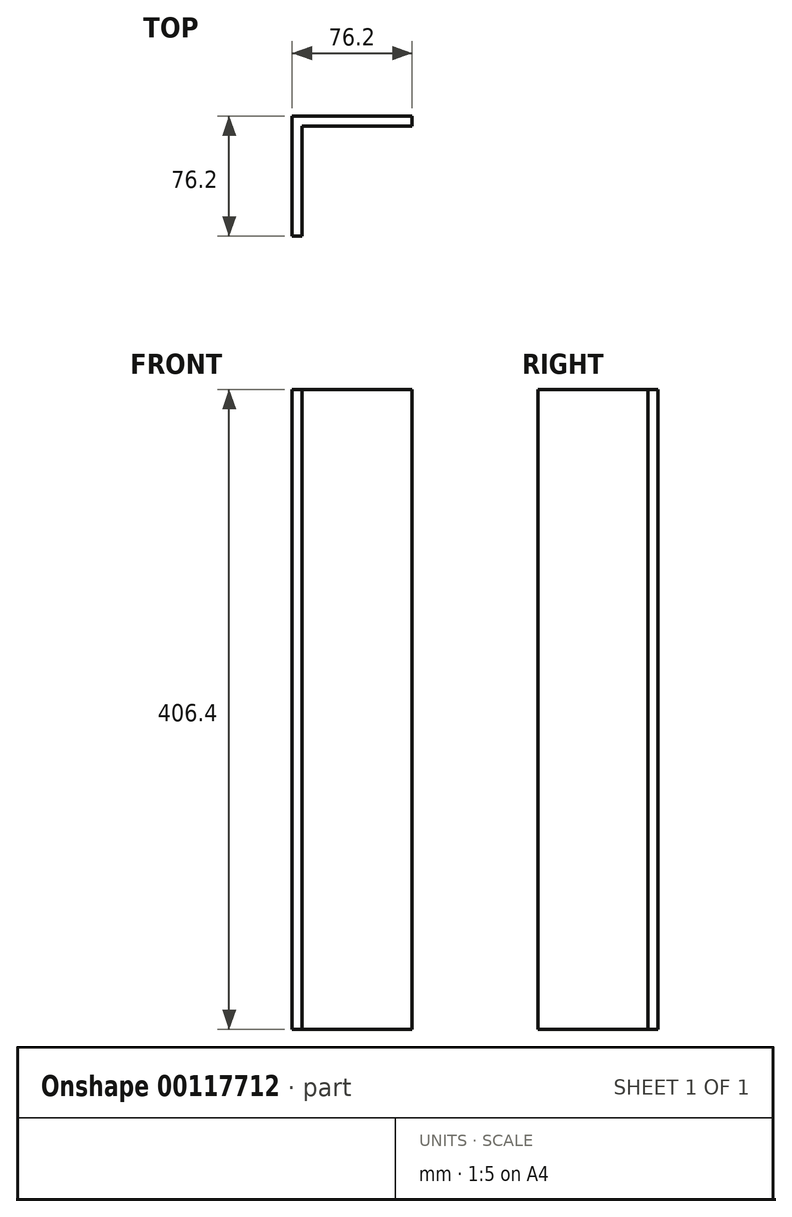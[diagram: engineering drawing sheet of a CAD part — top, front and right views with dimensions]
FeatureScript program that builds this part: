
annotation { "Feature Type Name" : "Feature", "Feature Type Description" : "" }
export const myFeature = defineFeature(function(context is Context, id is Id, definition is map)
    precondition{}
    {
        {
            var Q0;
            Q0=qCreatedBy(makeId("Top.planeOp"),FACE);
            var sketch = newSketch(context, id + "F0", { "sketchPlane" : qUnion([Q0])});
            skLineSegment(sketch, "E0", {"start": v(48.68, 27.52) * mm, "end": v(-27.52, 27.52) * mm});
            skLineSegment(sketch, "E1", {"start": v(-27.52, 27.52) * mm, "end": v(-27.52, -48.68) * mm});
            skLineSegment(sketch, "E2.0", {"start": v(-21.17, 21.17) * mm, "end": v(-21.17, -48.68) * mm});
            skLineSegment(sketch, "E2.1", {"start": v(48.68, 21.17) * mm, "end": v(-21.17, 21.17) * mm});
            skLineSegment(sketch, "E3", {"start": v(-27.52, -48.68) * mm, "end": v(-21.17, -48.68) * mm});
            skLineSegment(sketch, "E4", {"start": v(48.68, 27.52) * mm, "end": v(48.68, 21.17) * mm});
            skSolve(sketch);
        }
        {
            var Q0;
            Q0=makeQuery(id+"F0.imprint","IMPRINT",FACE,{"disambiguationData":[TD([[makeQuery(id+"F0.imprint","IMPRINT",EDGE,{"derivedFrom":sQuery(id+"F0.wireOp",EDGE,"E0")}),1.0]])]});
            extrude(context, id + "F1", {"entities" : qUnion([Q0]), "depth" : 406.4 * mm});
        }
    });
